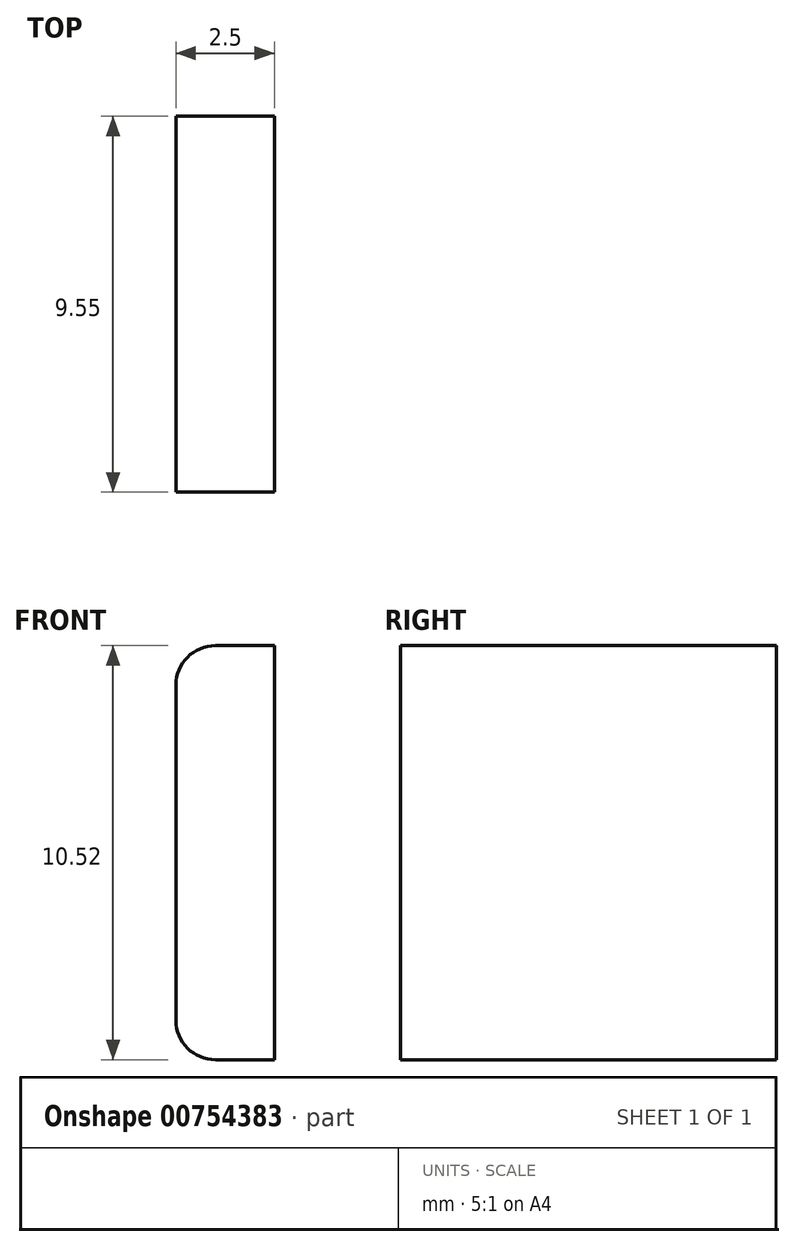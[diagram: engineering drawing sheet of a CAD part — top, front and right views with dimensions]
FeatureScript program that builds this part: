
annotation { "Feature Type Name" : "Feature", "Feature Type Description" : "" }
export const myFeature = defineFeature(function(context is Context, id is Id, definition is map)
    precondition{}
    {
        {
            var Q0;
            Q0=qCreatedBy(makeId("Front.planeOp"),FACE);
            var sketch = newSketch(context, id + "F0", { "sketchPlane" : qUnion([Q0])});
            skLineSegment(sketch, "E0", {"start": v(0, 0) * mm, "end": v(0, -5) * mm});
            skLineSegment(sketch, "E1", {"start": v(0, 0) * mm, "end": v(0, 5.52) * mm});
            skLineSegment(sketch, "E2", {"start": v(0, -5) * mm, "end": v(-1.5, -5) * mm});
            skLineSegment(sketch, "E3", {"start": v(0, 5.52) * mm, "end": v(-1.5, 5.52) * mm});
            skLineSegment(sketch, "E4", {"start": v(-2.5, 4.52) * mm, "end": v(-2.5, -4) * mm});
            skPoint(sketch, "E5.visualSharp", {"position": v(-2.5, 5.52) * mm});
            skArc(sketch, "E5.filletArc", {"start": v(-1.5, 5.52) * mm, "mid": v(-2.2, 5.22) * mm, "end": v(-2.5, 4.52) * mm});
            skPoint(sketch, "E6.visualSharp", {"position": v(-2.5, -5) * mm});
            skArc(sketch, "E6.filletArc", {"start": v(-2.5, -4) * mm, "mid": v(-2.2, -4.7) * mm, "end": v(-1.5, -5) * mm});
            skSolve(sketch);
        }
        {
            var Q0;
            Q0 = qSketchRegion(id + "F0", true);
            extrude(context, id + "F1", {"entities" : qUnion([Q0]), "depth" : 9.55 * mm, "offsetDistance" : 25 * mm});
        }
    });
